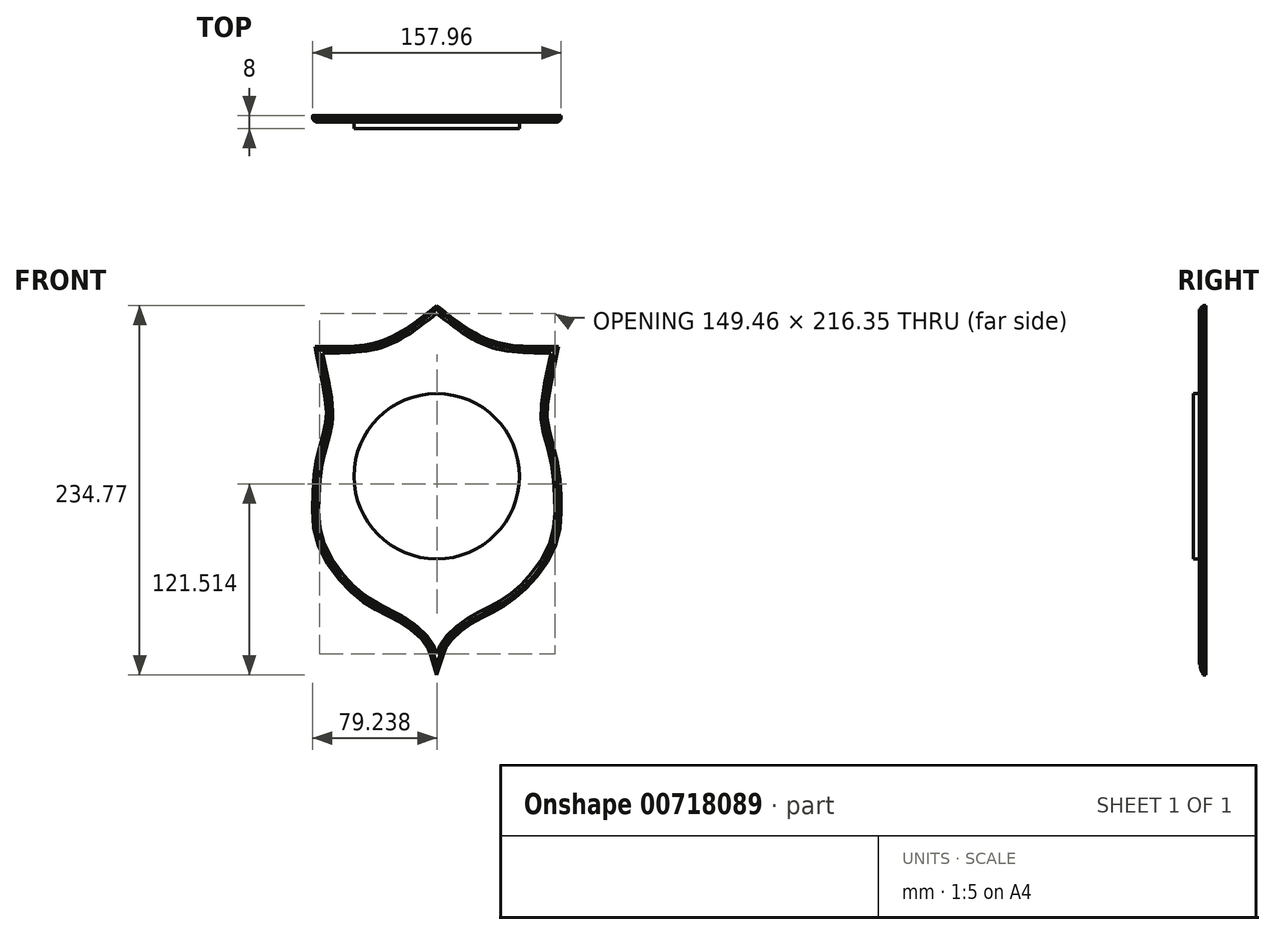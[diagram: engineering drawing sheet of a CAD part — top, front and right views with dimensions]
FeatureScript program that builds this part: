
annotation { "Feature Type Name" : "Feature", "Feature Type Description" : "" }
export const myFeature = defineFeature(function(context is Context, id is Id, definition is map)
    precondition{}
    {
        {
            var Q0;
            Q0=qCreatedBy(makeId("Front.planeOp"),FACE);
            var sketch = newSketch(context, id + "F0", { "sketchPlane" : qUnion([Q0])});
            skLineSegment(sketch, "E0", {"start": v(0, -112.97) * mm, "end": v(0, 103.38) * mm, "construction": true});
            skFitSpline(sketch, "E1", {"points": [v(0, 103.38) * mm, v(-33.18, 82.43) * mm, v(-72.47, 78.35) * mm], "startDerivative": vector(-63.47, -50.43) * mm, "endDerivative": vector(-81.45, 0.34) * mm});
            skFitSpline(sketch, "E2", {"points": [v(-72.47, 78.35) * mm, v(-66.59, 33.38) * mm, v(-72.47, 9.64) * mm, v(-74.91, -15.57) * mm, v(-72.47, -40.29) * mm, v(-58.02, -64.27) * mm, v(-43.58, -77) * mm, v(-29.88, -84.83) * mm, v(-16.66, -92.2) * mm, v(-3.7, -104.65) * mm, v(0, -112.97) * mm], "startDerivative": vector(111.62, -541.15) * mm, "endDerivative": vector(38.53, -123.34) * mm});
            skFitSpline(sketch, "E3.MirrorCS", {"points": [v(0, 103.38) * mm, v(33.18, 82.43) * mm, v(72.47, 78.35) * mm], "startDerivative": vector(63.47, -50.43) * mm, "endDerivative": vector(81.45, 0.34) * mm});
            skFitSpline(sketch, "E4.MirrorCS", {"points": [v(72.47, 78.35) * mm, v(66.59, 33.38) * mm, v(72.47, 9.64) * mm, v(74.91, -15.57) * mm, v(72.47, -40.29) * mm, v(58.02, -64.27) * mm, v(43.58, -77) * mm, v(29.88, -84.83) * mm, v(16.66, -92.2) * mm, v(3.7, -104.65) * mm, v(0, -112.97) * mm], "startDerivative": vector(-111.62, -541.15) * mm, "endDerivative": vector(-38.53, -123.34) * mm});
            skPoint(sketch, "E5", {"position": v(0, -4.8) * mm});
            skLineSegment(sketch, "E6", {"start": v(-75, 230) * mm, "end": v(-75, -223.9) * mm, "construction": true});
            skLineSegment(sketch, "E7.MirrorCS", {"start": v(75, 230) * mm, "end": v(75, -223.9) * mm, "construction": true});
            skCircle(sketch, "E8", {"center": v(0, 0) * mm, "radius": 52.5 * mm});
            skSolve(sketch);
        }
        {
            var Q0;
            Q0=qCreatedBy(makeId("Top.planeOp"),FACE);
            var sketch = newSketch(context, id + "F1", { "sketchPlane" : qUnion([Q0])});
            skLineSegment(sketch, "E9", {"start": v(-77.98, 0) * mm, "end": v(-73.98, 0) * mm});
            skLineSegment(sketch, "E10", {"start": v(-73.98, 0) * mm, "end": v(-73.98, -4) * mm});
            skLineSegment(sketch, "E11", {"start": v(-73.98, -4) * mm, "end": v(-75.98, -4) * mm});
            skLineSegment(sketch, "E12", {"start": v(-75.98, -4) * mm, "end": v(-75.98, -3.5) * mm});
            skLineSegment(sketch, "E13", {"start": v(-77.98, 0) * mm, "end": v(-77.98, -2) * mm});
            skLineSegment(sketch, "E14", {"start": v(-77.98, -2) * mm, "end": v(-77.48, -2) * mm});
            skArc(sketch, "E15", {"start": v(-77.48, -2) * mm, "mid": v(-77.04, -3.06) * mm, "end": v(-75.98, -3.5) * mm});
            skSolve(sketch);
        }
        {
            var Q0;
            Q0 = qSketchRegion(id + "F0", true);
            extrude(context, id + "F2", {"entities" : qUnion([Q0]), "depth" : 4 * mm, "offsetDistance" : 25 * mm});
        }
        {
            var Q0;
            Q0=makeQuery(id+"F0.imprint","IMPRINT",FACE,{"disambiguationData":[TD([[makeQuery(id+"F0.imprint","IMPRINT",EDGE,{"derivedFrom":sQuery(id+"F0.wireOp",EDGE,"E8")}),1.0]])]});
            extrude(context, id + "F3", {"entities" : qUnion([Q0]), "operationType" : NewBodyOperationType.ADD, "depth" : 8 * mm, "offsetDistance" : 25 * mm});
        }
        {
            var Q0;
            Q0 = qSketchRegion(id + "F1", true);
            var Q1;
            Q1=makeQuery(id+"F2.opExtrude","CAP_EDGE",EDGE,{"disambiguationData":[OSD([sQuery(id+"F0.wireOp",EDGE,"E2")])],"isStart":false});
            var Q2;
            Q2=makeQuery(id+"F2.opExtrude","CAP_EDGE",EDGE,{"disambiguationData":[OSD([sQuery(id+"F0.wireOp",EDGE,"E1")])],"isStart":false});
            var Q3;
            Q3=makeQuery(id+"F2.opExtrude","CAP_EDGE",EDGE,{"disambiguationData":[OSD([sQuery(id+"F0.wireOp",EDGE,"E3.MirrorCS")])],"isStart":false});
            var Q4;
            Q4=makeQuery(id+"F2.opExtrude","CAP_EDGE",EDGE,{"disambiguationData":[OSD([sQuery(id+"F0.wireOp",EDGE,"E4.MirrorCS")])],"isStart":false});
            sweep(context, id + "F4", {"profiles" : qUnion([Q0]), "path" : qUnion([Q1, Q2, Q3, Q4])});
        }
    });
